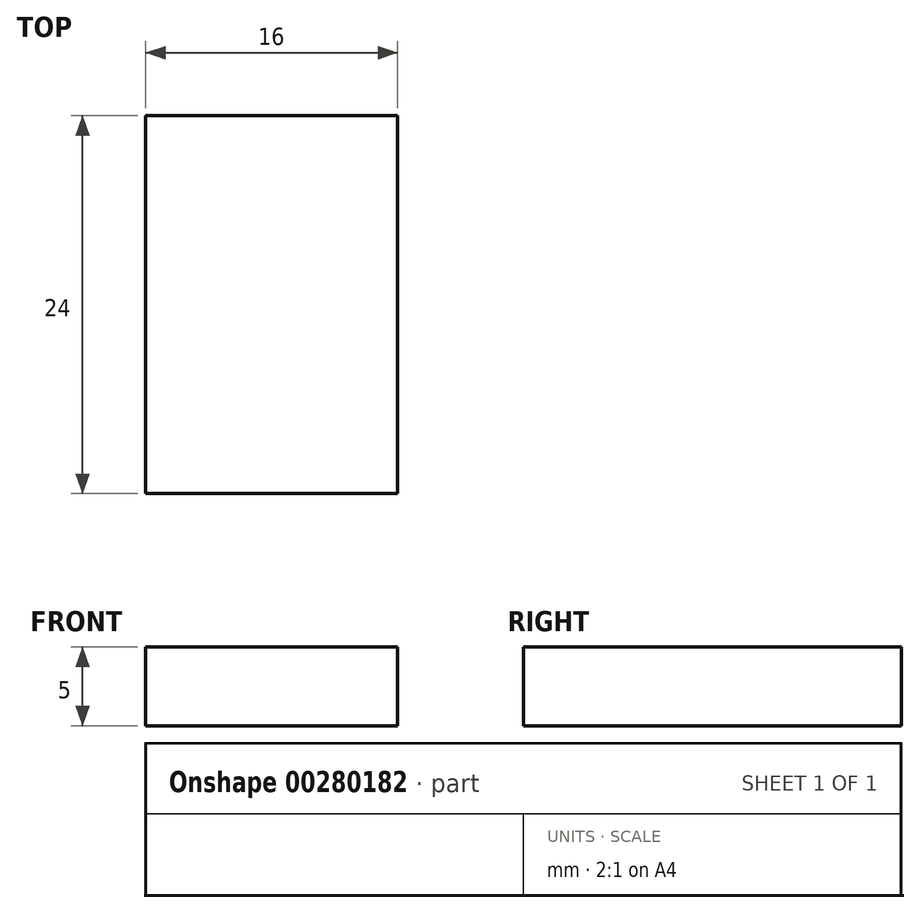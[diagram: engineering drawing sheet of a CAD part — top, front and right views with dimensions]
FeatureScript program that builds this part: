
annotation { "Feature Type Name" : "Feature", "Feature Type Description" : "" }
export const myFeature = defineFeature(function(context is Context, id is Id, definition is map)
    precondition{}
    {
        {
            var Q0;
            Q0=qCreatedBy(makeId("Front.planeOp"),FACE);
            var sketch = newSketch(context, id + "F0", { "sketchPlane" : qUnion([Q0])});
            skLineSegment(sketch, "E0.bottom", {"start": v(8, 2.5) * mm, "end": v(-8, 2.5) * mm});
            skLineSegment(sketch, "E0.top", {"start": v(8, -2.5) * mm, "end": v(-8, -2.5) * mm});
            skLineSegment(sketch, "E0.left", {"start": v(8, 2.5) * mm, "end": v(8, -2.5) * mm});
            skLineSegment(sketch, "E0.right", {"start": v(-8, 2.5) * mm, "end": v(-8, -2.5) * mm});
            skPoint(sketch, "E0.middle", {"position": v(0, 0) * mm});
            skSolve(sketch);
        }
        {
            var Q0;
            Q0 = qSketchRegion(id + "F0", true);
            extrude(context, id + "F1", {"entities" : qUnion([Q0]), "depth" : 24 * mm, "symmetric" : true});
        }
    });
